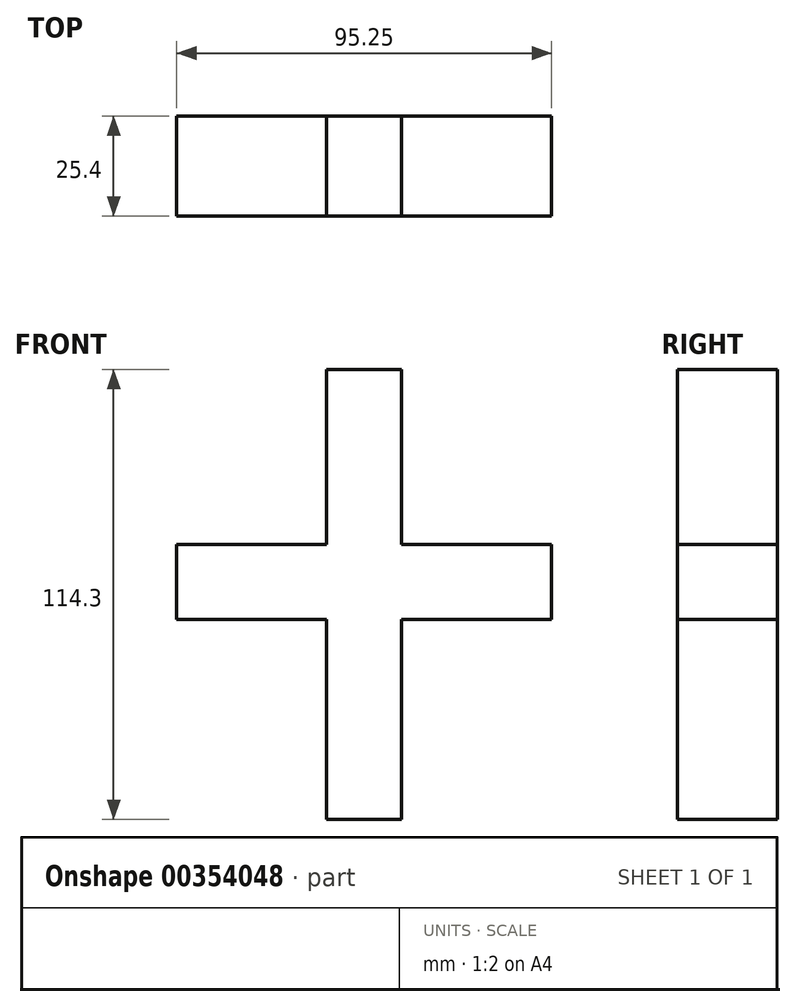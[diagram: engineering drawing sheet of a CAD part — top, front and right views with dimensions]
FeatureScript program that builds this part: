
annotation { "Feature Type Name" : "Feature", "Feature Type Description" : "" }
export const myFeature = defineFeature(function(context is Context, id is Id, definition is map)
    precondition{}
    {
        {
            var Q0;
            Q0=qCreatedBy(makeId("Front.planeOp"),FACE);
            var sketch = newSketch(context, id + "F0", { "sketchPlane" : qUnion([Q0])});
            skLineSegment(sketch, "E0", {"start": v(-22.27, 44.45) * mm, "end": v(-3.22, 44.45) * mm});
            skLineSegment(sketch, "E1", {"start": v(-3.22, 44.45) * mm, "end": v(-3.22, 0) * mm});
            skLineSegment(sketch, "E2", {"start": v(-3.22, 0) * mm, "end": v(34.88, 0) * mm});
            skLineSegment(sketch, "E3", {"start": v(34.88, 0) * mm, "end": v(34.88, -19.05) * mm});
            skLineSegment(sketch, "E4", {"start": v(34.88, -19.05) * mm, "end": v(-3.22, -19.05) * mm});
            skLineSegment(sketch, "E5", {"start": v(-3.22, -19.05) * mm, "end": v(-3.22, -69.85) * mm});
            skLineSegment(sketch, "E6", {"start": v(-3.22, -69.85) * mm, "end": v(-22.27, -69.85) * mm});
            skLineSegment(sketch, "E7", {"start": v(-22.27, -69.85) * mm, "end": v(-22.27, -19.05) * mm});
            skLineSegment(sketch, "E8", {"start": v(-22.27, -19.05) * mm, "end": v(-60.37, -19.05) * mm});
            skLineSegment(sketch, "E9", {"start": v(-60.37, -19.05) * mm, "end": v(-60.37, 0) * mm});
            skLineSegment(sketch, "E10", {"start": v(-60.37, 0) * mm, "end": v(-22.27, 0) * mm});
            skLineSegment(sketch, "E11", {"start": v(-22.27, 0) * mm, "end": v(-22.27, 44.45) * mm});
            skSolve(sketch);
        }
        {
            var Q0;
            Q0=makeQuery(id+"F0.imprint","IMPRINT",FACE,{"disambiguationData":[TD([[makeQuery(id+"F0.imprint","IMPRINT",EDGE,{"derivedFrom":sQuery(id+"F0.wireOp",EDGE,"E0")}),-1.0]])]});
            extrude(context, id + "F1", {"entities" : qUnion([Q0]), "depth" : 25.4 * mm});
        }
    });
